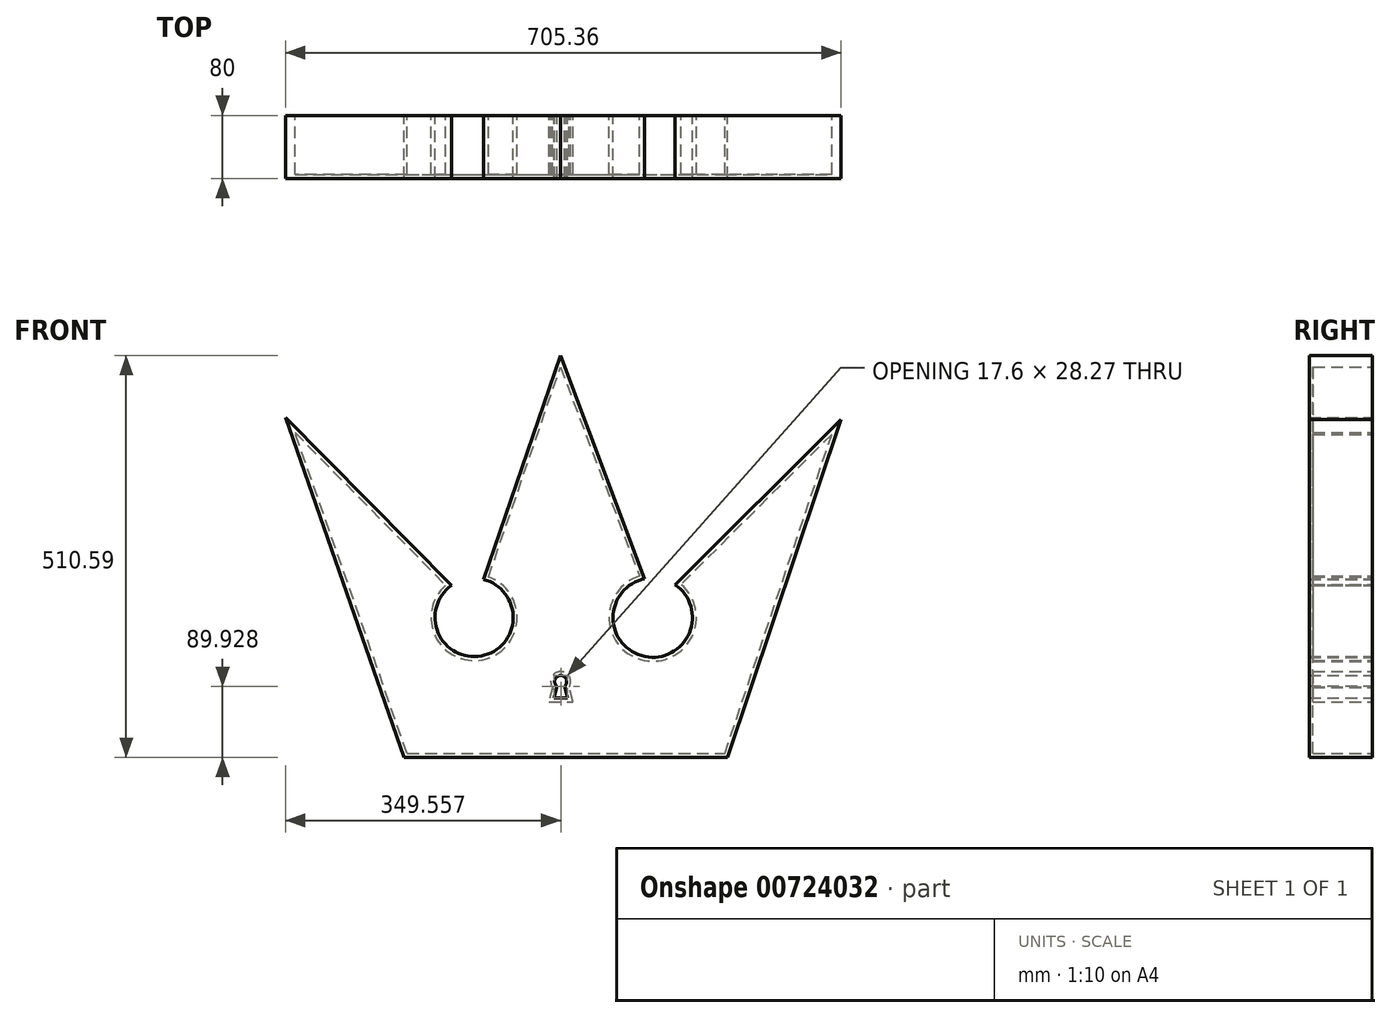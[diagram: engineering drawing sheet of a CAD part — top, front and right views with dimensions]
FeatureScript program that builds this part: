
annotation { "Feature Type Name" : "Feature", "Feature Type Description" : "" }
export const myFeature = defineFeature(function(context is Context, id is Id, definition is map)
    precondition{}
    {
        {
            var Q0;
            Q0=qCreatedBy(makeId("Front.planeOp"),FACE);
            var sketch = newSketch(context, id + "F0", { "sketchPlane" : qUnion([Q0])});
            skLineSegment(sketch, "E0", {"start": v(-198.14, -82.86) * mm, "end": v(212.52, -82.86) * mm});
            skLineSegment(sketch, "E1", {"start": v(212.52, -82.86) * mm, "end": v(356.5, 346.16) * mm});
            skLineSegment(sketch, "E2", {"start": v(356.5, 346.16) * mm, "end": v(145.85, 136.48) * mm});
            skLineSegment(sketch, "E3", {"start": v(-198.14, -82.86) * mm, "end": v(-348.87, 349.05) * mm});
            skLineSegment(sketch, "E4", {"start": v(-348.87, 349.05) * mm, "end": v(-138.23, 135.51) * mm});
            skArc(sketch, "E5", {"start": v(-138.23, 135.51) * mm, "mid": v(-100.17, 46.07) * mm, "end": v(-97.65, 143.24) * mm});
            skArc(sketch, "E6", {"start": v(107.2, 144.2) * mm, "mid": v(107.53, 45.37) * mm, "end": v(145.85, 136.48) * mm});
            skLineSegment(sketch, "E7", {"start": v(-97.65, 143.24) * mm, "end": v(0, 427.73) * mm});
            skLineSegment(sketch, "E8", {"start": v(0, 427.73) * mm, "end": v(107.2, 144.2) * mm});
            skCircle(sketch, "E9", {"center": v(0.52, 13.55) * mm, "radius": 7.65 * mm});
            skLineSegment(sketch, "E10", {"start": v(-4.45, 7.73) * mm, "end": v(-8.11, -7.07) * mm});
            skLineSegment(sketch, "E11", {"start": v(-8.11, -7.07) * mm, "end": v(9.49, -7.07) * mm});
            skLineSegment(sketch, "E12", {"start": v(9.49, -7.07) * mm, "end": v(5.66, 7.88) * mm});
            skSolve(sketch);
        }
        {
            var Q0;
            Q0 = qSketchRegion(id + "F0", true);
            var Q1;
            Q1=makeQuery(id+"F0.imprint","IMPRINT",FACE,{"disambiguationData":[TD([[makeQuery(id+"F0.imprint","IMPRINT",EDGE,{"derivedFrom":sQuery(id+"F0.wireOp",EDGE,"E0")}),1.0]])]});
            extrude(context, id + "F1", {"entities" : qUnion([Q0, Q1]), "depth" : 80 * mm, "offsetDistance" : 25 * mm});
        }
        {
            var Q0;
            Q0=makeQuery(id+"F1.opExtrude","CAP_FACE",FACE,{"disambiguationData":[OSD([sQuery(id+"F0.wireOp",EDGE,"E0"),sQuery(id+"F0.wireOp",EDGE,"E1"),sQuery(id+"F0.wireOp",EDGE,"E2"),sQuery(id+"F0.wireOp",EDGE,"E3"),sQuery(id+"F0.wireOp",EDGE,"E4"),sQuery(id+"F0.wireOp",EDGE,"E5"),sQuery(id+"F0.wireOp",EDGE,"E6"),sQuery(id+"F0.wireOp",EDGE,"E7"),sQuery(id+"F0.wireOp",EDGE,"E8")])],"isStart":true});
            shell(context, id + "F2", {"entities" : qUnion([Q0]), "thickness" : 5 * mm});
        }
    });
